# Revit family: Hand_Dryer-World_Dryer-VERDEdri
name_source: partatom
category: Mechanical Equipment
revit_build: Autodesk Revit Architecture 2015 (Build: 20140606_1530(x64)
units: mm (PartAtom-declared; Revit-internal decimal feet)

## types (1)
- Not A Type - Load Type Catalog
    ADA Compliant = Yes
    Activation = Automatic IR Optical Sensor
    Air Filtration = HEPA
    Air Temperature = 130F (57C) @ 70F (21C) room temp
    Air Velocity = 225 MPH / 19,800 LFM
    Apparent Load = 950 VA
    Certifications = cETLus, CE
    Cover Finish = Metal - World Dryer - Aluminum - White
    Depth = 3' - 10 13/16"
    Description = Hand Dryer
    Electrical Current = 8 A
    Frequency = 50 Hz
    Height = 13' - 3 19/32"
    Ingress Protection = IP24
    Manufacturer = Worl Dryer
    Model = VERDEdri
    Motor Power = 5/8 HP
    Motor Speed (RPM) = 31000
    Mounting = Surface Mounted
    Number of Poles = 1
    Power Factor = 1
    Product Documentation Link = http://www.worlddryer.com
    Product Name = VERDEdri
    Product Page URL = http://worlddryer.com
    Product data url = https://bimobject.com
    Speed Control = Hi/Low
Hi/Low
    URL = http://worlddryer.com
    Voltage = 120 V
    Wattage = 950 W
    Width = 11' - 7 3/16"
    Wire Guage = 14

## geometry (parser evidence)
native form markers: Blend x2, Sweep x5
no freeform markers — native parametric forms only
